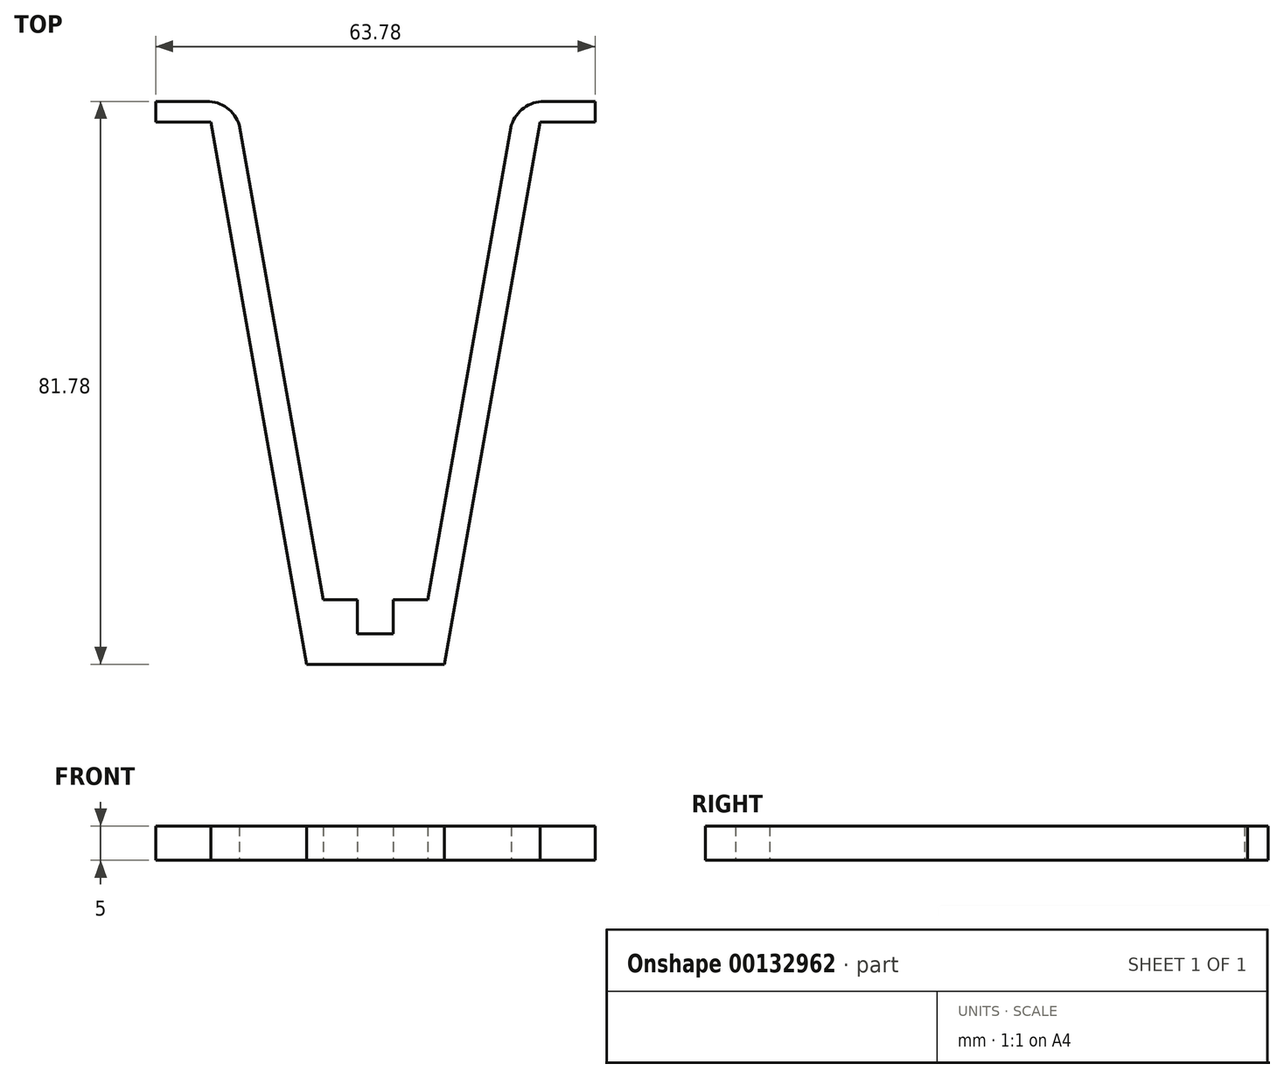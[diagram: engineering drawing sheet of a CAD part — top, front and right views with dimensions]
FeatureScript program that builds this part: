
annotation { "Feature Type Name" : "Feature", "Feature Type Description" : "" }
export const myFeature = defineFeature(function(context is Context, id is Id, definition is map)
    precondition{}
    {
        {
            var Q0;
            Q0=qCreatedBy(makeId("Top.planeOp"),FACE);
            var sketch = newSketch(context, id + "F0", { "sketchPlane" : qUnion([Q0])});
            skLineSegment(sketch, "E0", {"start": v(0, 0) * mm, "end": v(-10, 0) * mm});
            skLineSegment(sketch, "E1", {"start": v(-10, 0) * mm, "end": v(-23.9, 78.78) * mm});
            skLineSegment(sketch, "E2", {"start": v(-19.76, 78.33) * mm, "end": v(-7.6, 9.4) * mm});
            skLineSegment(sketch, "E3", {"start": v(-7.6, 9.4) * mm, "end": v(-2.6, 9.4) * mm});
            skLineSegment(sketch, "E4", {"start": v(-2.6, 9.4) * mm, "end": v(-2.6, 4.4) * mm});
            skLineSegment(sketch, "E5", {"start": v(-2.6, 4.4) * mm, "end": v(0, 4.4) * mm});
            skLineSegment(sketch, "E6.MirrorCS", {"start": v(19.76, 78.33) * mm, "end": v(7.6, 9.4) * mm});
            skLineSegment(sketch, "E7.MirrorCS", {"start": v(10, 0) * mm, "end": v(23.9, 78.78) * mm});
            skLineSegment(sketch, "E8.MirrorCS", {"start": v(7.6, 9.4) * mm, "end": v(2.6, 9.4) * mm});
            skLineSegment(sketch, "E9.MirrorCS", {"start": v(2.6, 9.4) * mm, "end": v(2.6, 4.4) * mm});
            skLineSegment(sketch, "E10.MirrorCS", {"start": v(0, 0) * mm, "end": v(10, 0) * mm});
            skLineSegment(sketch, "E11.MirrorCS", {"start": v(2.6, 4.4) * mm, "end": v(0, 4.4) * mm});
            skLineSegment(sketch, "E12", {"start": v(-23.9, 78.78) * mm, "end": v(-31.9, 78.78) * mm});
            skLineSegment(sketch, "E13", {"start": v(-31.9, 78.78) * mm, "end": v(-31.9, 81.78) * mm});
            skLineSegment(sketch, "E14", {"start": v(-31.9, 81.78) * mm, "end": v(-19.76, 81.78) * mm});
            skLineSegment(sketch, "E15", {"start": v(-19.76, 78.33) * mm, "end": v(-19.76, 81.78) * mm});
            skLineSegment(sketch, "E16.MirrorCS", {"start": v(31.9, 81.78) * mm, "end": v(19.76, 81.78) * mm});
            skLineSegment(sketch, "E17.MirrorCS", {"start": v(31.9, 78.78) * mm, "end": v(31.9, 81.78) * mm});
            skLineSegment(sketch, "E18.MirrorCS", {"start": v(23.9, 78.78) * mm, "end": v(31.9, 78.78) * mm});
            skLineSegment(sketch, "E19.MirrorCS", {"start": v(19.76, 78.33) * mm, "end": v(19.76, 81.78) * mm});
            skPoint(sketch, "E20.MirrorCS.end.orphan", {"position": v(19.76, 78.33) * mm});
            skPoint(sketch, "E20.MirrorCS.start.orphan", {"position": v(23.9, 78.78) * mm});
            skSolve(sketch);
        }
        {
            var Q0;
            Q0=makeQuery(id+"F0.imprint","IMPRINT",FACE,{"disambiguationData":[TD([[makeQuery(id+"F0.imprint","IMPRINT",EDGE,{"derivedFrom":sQuery(id+"F0.wireOp",EDGE,"E0")}),-1.0]])]});
            extrude(context, id + "F1", {"entities" : qUnion([Q0]), "depth" : 5 * mm});
        }
        {
            var Q0;
            Q0=makeQuery(id+"F1.opExtrude","SWEPT_EDGE",EDGE,{"disambiguationData":[OSD([sQuery(id+"F0.wireOp",EDGE,"E14"),sQuery(id+"F0.wireOp",EDGE,"E15")])]});
            var Q1;
            Q1=makeQuery(id+"F1.opExtrude","SWEPT_EDGE",EDGE,{"disambiguationData":[OSD([sQuery(id+"F0.wireOp",EDGE,"E16.MirrorCS"),sQuery(id+"F0.wireOp",EDGE,"E19.MirrorCS")])]});
            fillet(context, id + "F2", {"entities" : qUnion([Q0, Q1]), "radius" : 5 * mm, "tangentPropagation" : true, "allowEdgeOverflow" : false});
        }
    });
